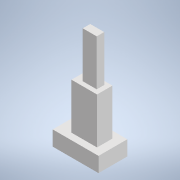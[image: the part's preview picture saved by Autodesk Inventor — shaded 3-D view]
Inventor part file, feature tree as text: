
AUTODESK INVENTOR PART (.ipt)
format: ipt  version: 2020 (Build 240168000, 168)  size: 105,984 bytes
history: native  units: in
note: dims shown in document units (in); Inventor stores cm internally (conversion verified against a paired STEP export)
features: extrude x3, sketch x3
ambient origin geometry x8: Origin, YZ Plane, XZ Plane, XY Plane, X Axis, Y Axis, Z Axis, Center Point
bodies: Solid1 (feature_tree)
feature tree (6):
  extrude  "Extrusion1"  Depth=1.0in TaperAngle=0.0deg
  extrude  "Extrusion2"  [1 undecoded]
  extrude  "Extrusion3"  [1 undecoded]
  sketch  "Sketch1"  dims[d0=1.0in d1=0.0in d2=1.0in d3=0.0in]
  sketch  "Sketch2"  dims[d4=1.0in d5=0.0in]
  sketch  "Sketch3"
note: 2 required parameter values undecoded (feature->parameter linkage not recoverable at this tier; creation-order binding heuristic only, values carry confidence <= 0.55)
